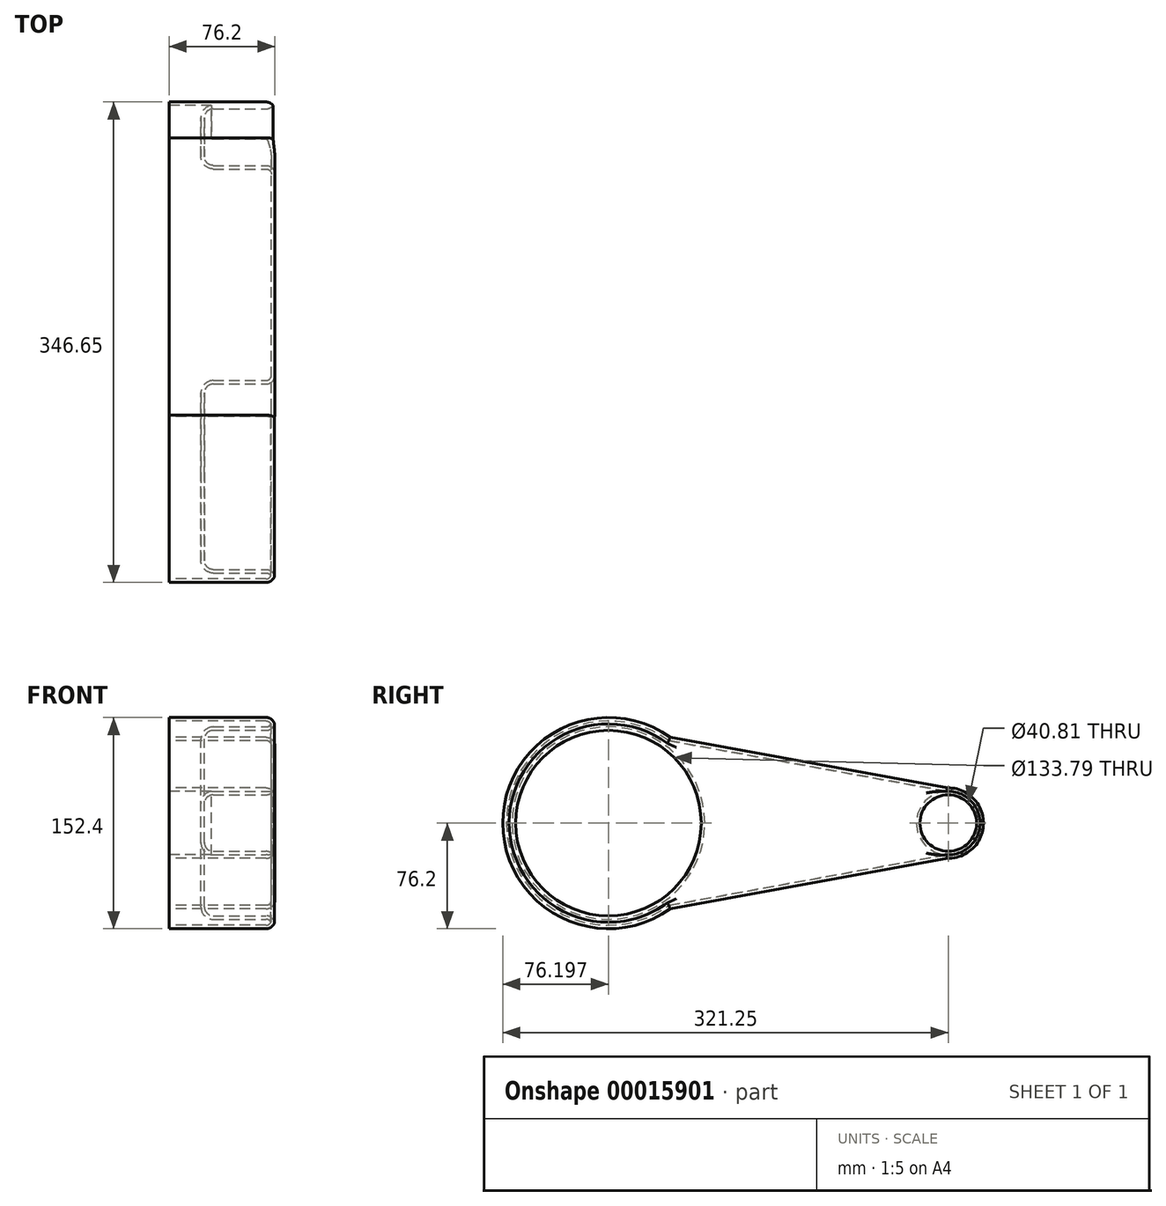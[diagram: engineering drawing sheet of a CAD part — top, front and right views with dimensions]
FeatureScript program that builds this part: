
annotation { "Feature Type Name" : "Feature", "Feature Type Description" : "" }
export const myFeature = defineFeature(function(context is Context, id is Id, definition is map)
    precondition{}
    {
        {
            var Q0;
            Q0=qCreatedBy(makeId("Right.planeOp"),FACE);
            var sketch = newSketch(context, id + "F0", { "sketchPlane" : qUnion([Q0])});
            skCircle(sketch, "E0", {"center": v(-140.55, 0) * mm, "radius": 76.2 * mm});
            skCircle(sketch, "E1", {"center": v(104.5, 0) * mm, "radius": 25.4 * mm});
            skLineSegment(sketch, "E2", {"start": v(-96.05, 61.86) * mm, "end": v(103.85, 25.4) * mm});
            skLineSegment(sketch, "E3.MirrorCS", {"start": v(-96.05, -61.86) * mm, "end": v(103.85, -25.4) * mm});
            skSolve(sketch);
        }
        {
            var Q0;
            {var subQ0=sQuery(id+"F0.wireOp",EDGE,"E0");var subQ2=makeQuery(id+"F0.imprint","INTERSECT",VERTEX,{"derivedFrom":[subQ0,sQuery(id+"F0.wireOp",EDGE,"E3.MirrorCS")]});Q0=makeQuery(id+"F0.imprint","IMPRINT",FACE,{"disambiguationData":[TD([[makeQuery(id+"F0.imprint","IMPRINT",EDGE,{"disambiguationData":[TD([[subQ2,1.0]])],"derivedFrom":subQ0}),1.0]])]});}
            var Q1;
            {var subQ1=sQuery(id+"F0.wireOp",EDGE,"E3.MirrorCS");Q1=makeQuery(id+"F0.imprint","IMPRINT",FACE,{"disambiguationData":[TD([[makeQuery(id+"F0.imprint","IMPRINT",EDGE,{"derivedFrom":subQ1}),1.0]])]});}
            var Q2;
            {var subQ0=sQuery(id+"F0.wireOp",EDGE,"E1");var subQ2=makeQuery(id+"F0.imprint","INTERSECT",VERTEX,{"derivedFrom":[subQ0,sQuery(id+"F0.wireOp",EDGE,"E3.MirrorCS")]});Q2=makeQuery(id+"F0.imprint","IMPRINT",FACE,{"disambiguationData":[TD([[makeQuery(id+"F0.imprint","IMPRINT",EDGE,{"disambiguationData":[TD([[subQ2,1.0]])],"derivedFrom":subQ0}),1.0]])]});}
            extrude(context, id + "F1", {"entities" : qUnion([Q0, Q1, Q2]), "depth" : 76.2 * mm});
        }
        {
            var Q0;
            Q0=makeQuery(id+"F1.opExtrude","CAP_FACE",FACE,{"disambiguationData":[OSD([sQuery(id+"F0.wireOp",EDGE,"E0"),sQuery(id+"F0.wireOp",EDGE,"E1"),sQuery(id+"F0.wireOp",EDGE,"E3.MirrorCS"),sQuery(id+"F0.wireOp",EDGE,"E2")])],"isStart":false});
            var sketch = newSketch(context, id + "F2", { "sketchPlane" : qUnion([Q0])});
            skCircle(sketch, "E4", {"center": v(-140.55, 0) * mm, "radius": 66.9 * mm});
            skCircle(sketch, "E5", {"center": v(104.5, 0) * mm, "radius": 20.4 * mm});
            skSolve(sketch);
        }
        {
            var Q0;
            Q0=makeQuery(id+"F2.imprint","IMPRINT",FACE,{"disambiguationData":[TD([[makeQuery(id+"F2.imprint","IMPRINT",EDGE,{"derivedFrom":sQuery(id+"F2.wireOp",EDGE,"E4")}),1.0]])]});
            var Q1;
            Q1=makeQuery(id+"F2.imprint","IMPRINT",FACE,{"disambiguationData":[TD([[makeQuery(id+"F2.imprint","IMPRINT",EDGE,{"derivedFrom":sQuery(id+"F2.wireOp",EDGE,"E5")}),1.0]])]});
            extrude(context, id + "F3", {"entities" : qUnion([Q0, Q1]), "operationType" : NewBodyOperationType.REMOVE, "oppositeDirection" : true, "depth" : 50.8 * mm});
        }
        {
            var Q0;
            Q0=makeQuery(id+"F1.opExtrude","CAP_FACE",FACE,{"disambiguationData":[OSD([sQuery(id+"F0.wireOp",EDGE,"E0"),sQuery(id+"F0.wireOp",EDGE,"E1"),sQuery(id+"F0.wireOp",EDGE,"E3.MirrorCS"),sQuery(id+"F0.wireOp",EDGE,"E2")])],"isStart":false});
            var Q1;
            Q1=makeQuery(id+"F3.boolean.opBoolean","COPY",EDGE,{"derivedFrom":makeQuery(id+"F3.opExtrude","CAP_EDGE",EDGE,{"disambiguationData":[OSD([sQuery(id+"F2.wireOp",EDGE,"E4")])],"isStart":false})});
            var Q2;
            Q2=makeQuery(id+"F3.boolean.opBoolean","COPY",EDGE,{"derivedFrom":makeQuery(id+"F3.opExtrude","CAP_EDGE",EDGE,{"disambiguationData":[OSD([sQuery(id+"F2.wireOp",EDGE,"E5")])],"isStart":false})});
            fillet(context, id + "F4", {"entities" : qUnion([Q0, Q1, Q2]), "radius" : 6.35 * mm, "tangentPropagation" : true, "allowEdgeOverflow" : false});
        }
        {
            var Q0;
            Q0=makeQuery(id+"F1.opExtrude","CAP_FACE",FACE,{"disambiguationData":[OSD([sQuery(id+"F0.wireOp",EDGE,"E0"),sQuery(id+"F0.wireOp",EDGE,"E1"),sQuery(id+"F0.wireOp",EDGE,"E3.MirrorCS"),sQuery(id+"F0.wireOp",EDGE,"E2")])],"isStart":true});
            shell(context, id + "F5", {"entities" : qUnion([Q0]), "thickness" : 2.54 * mm});
        }
    });
